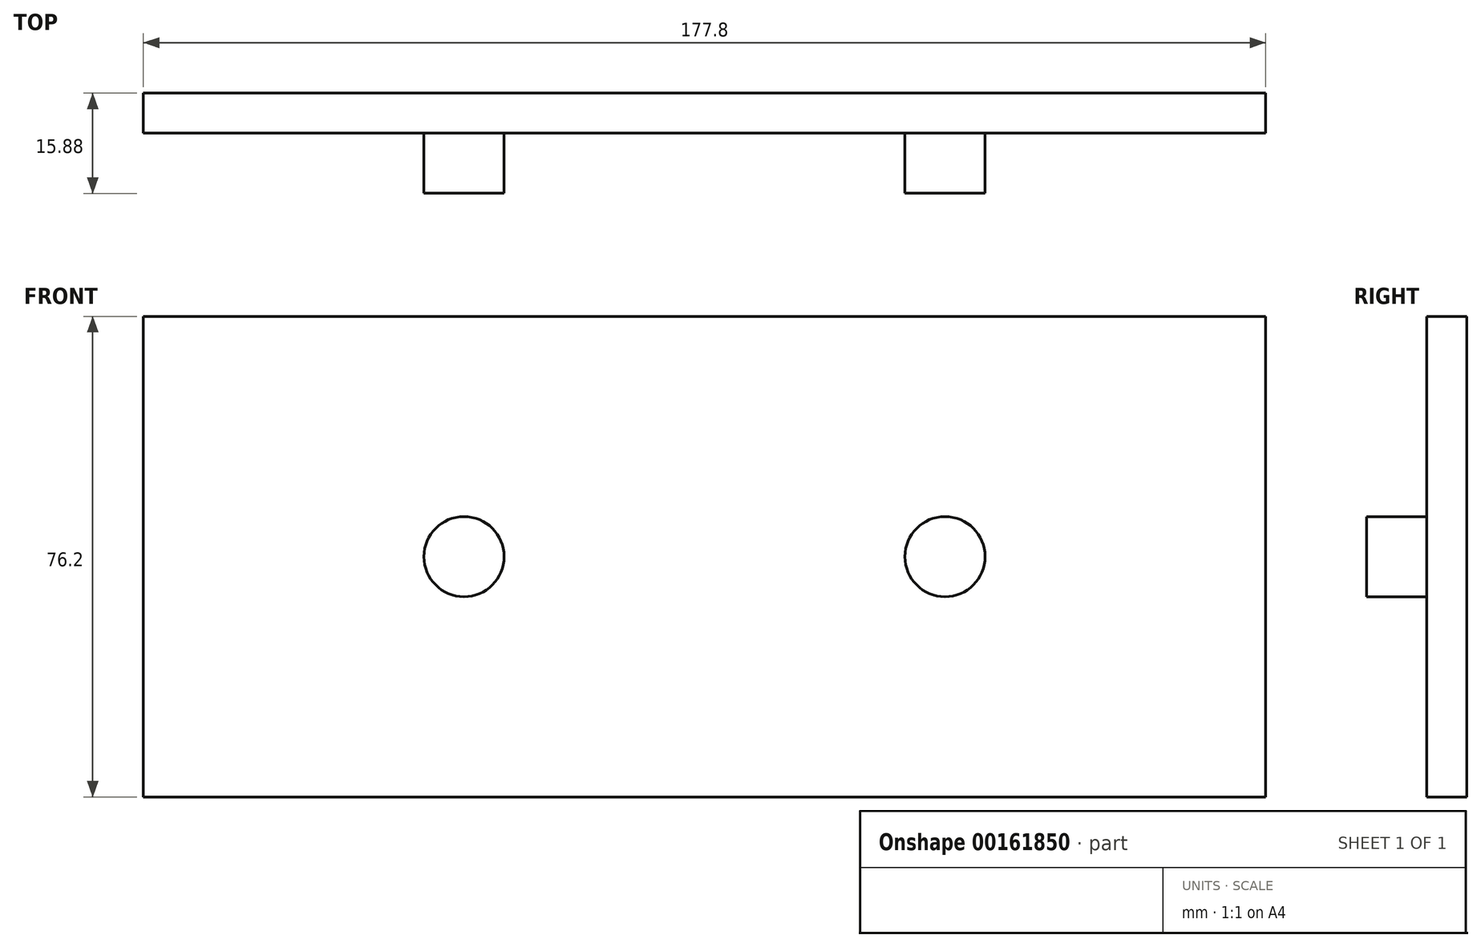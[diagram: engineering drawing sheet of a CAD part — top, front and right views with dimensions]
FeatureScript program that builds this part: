
annotation { "Feature Type Name" : "Feature", "Feature Type Description" : "" }
export const myFeature = defineFeature(function(context is Context, id is Id, definition is map)
    precondition{}
    {
        {
            var Q0;
            Q0=qCreatedBy(makeId("Front.planeOp"),FACE);
            var sketch = newSketch(context, id + "F0", { "sketchPlane" : qUnion([Q0])});
            skLineSegment(sketch, "E0.bottom", {"start": v(0, 0) * mm, "end": v(177.8, 0) * mm});
            skLineSegment(sketch, "E0.top", {"start": v(0, -76.2) * mm, "end": v(177.8, -76.2) * mm});
            skLineSegment(sketch, "E0.left", {"start": v(0, 0) * mm, "end": v(0, -76.2) * mm});
            skLineSegment(sketch, "E0.right", {"start": v(177.8, 0) * mm, "end": v(177.8, -76.2) * mm});
            skSolve(sketch);
        }
        {
            var Q0;
            Q0=qSketchRegion(id+"F0",true);
            extrude(context, id + "F1", {"entities" : qUnion([Q0]), "depth" : 6.35 * mm});
        }
        {
            var Q0;
            Q0=makeQuery(id+"F1.opExtrude","CAP_FACE",FACE,{"disambiguationData":[OSD([sQuery(id+"F0.wireOp",EDGE,"E0.bottom"),sQuery(id+"F0.wireOp",EDGE,"E0.top"),sQuery(id+"F0.wireOp",EDGE,"E0.left"),sQuery(id+"F0.wireOp",EDGE,"E0.right")])],"isStart":false});
            var sketch = newSketch(context, id + "F2", { "sketchPlane" : qUnion([Q0])});
            skLineSegment(sketch, "E1", {"start": v(0, -38.1) * mm, "end": v(177.8, -38.1) * mm});
            skLineSegment(sketch, "E2", {"start": v(50.8, 0) * mm, "end": v(50.8, -76.2) * mm});
            skLineSegment(sketch, "E3", {"start": v(127, 0) * mm, "end": v(127, -76.2) * mm});
            skCircle(sketch, "E4", {"center": v(50.8, -38.1) * mm, "radius": 6.35 * mm});
            skCircle(sketch, "E5", {"center": v(127, -38.1) * mm, "radius": 6.35 * mm});
            skSolve(sketch);
        }
        {
            var Q0;
            Q0=qSketchRegion(id+"F2",true);
            extrude(context, id + "F3", {"entities" : qUnion([Q0]), "operationType" : NewBodyOperationType.ADD, "depth" : 9.52 * mm});
        }
    });
